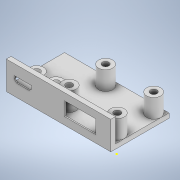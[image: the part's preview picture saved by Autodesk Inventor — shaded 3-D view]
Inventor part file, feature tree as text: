
AUTODESK INVENTOR PART (.ipt)
format: ipt  version: 2022 (Build 260153000, 153)  size: 289,280 bytes
history: native  units: mm
features: sketch x14, extrude x13
ambient origin geometry x8: Origin, YZ Plane, XZ Plane, XY Plane, X Axis, Y Axis, Z Axis, Center Point
bodies: Solid1 (feature_tree)
feature tree (27):
  extrude  "Extrusion1"  Depth=25.0mm
  extrude  "Extrusion2"  Depth=2.0mm
  extrude  "Extrusion3"  Depth=20.5mm
  extrude  "Extrusion4"  TaperAngle=0.0deg  [1 undecoded]
  extrude  "Extrusion5"  Depth=6.0mm
  extrude  "Extrusion6"  Depth=6.0mm
  extrude  "Extrusion7"  Depth=5.0mm
  extrude  "Extrusion8"  Depth=8.0mm TaperAngle=0.0deg
  extrude  "Extrusion9"  Depth=2.8mm
  extrude  "Extrusion10"  Depth=2.8mm
  extrude  "Extrusion11"  Depth=5.8mm
  extrude  "Extrusion12"  Depth=10.0mm TaperAngle=0.0deg
  extrude  "Extrusion13"  Depth=5.8mm
  sketch  "Sketch18"  dims[d36=1.0mm d37=8.3mm d38=10.0mm d39=0.0mm d40=100.0mm d41=0.0mm d42=16.0mm d43=1.3mm d44=1.5mm d45=1.5mm d46=0.0mm d49=18.0mm d50=2.0mm d51=0.0mm d52=2.0mm d53=0.0mm d54=14.0mm d55=10.0mm d56=10.0mm d57=8.3mm d58=6.0mm d59=6.0mm d60=2.85mm d61=1.9mm d62=0.0mm d63=3.0mm d64=3.0mm d65=4.0mm d66=0.0mm d68=7.4mm d69=2.3mm d70=2.65mm d71=1.4mm d75=1.0mm d76=1.0mm d77=135.0deg d78=4.0mm d79=0.0mm d80=1.6mm d81=8.0mm d82=1.0mm d83=1.0mm d84=1.0mm d85=1.5mm d86=0.0mm]
  sketch  "Sketch1"  dims[d0=30.0mm d1=25.0mm]
  sketch  "Sketch2"  dims[d2=2.0mm d3=0.0mm d4=15.5mm]
  sketch  "Sketch3"  dims[d5=15.5mm d6=20.5mm]
  sketch  "Sketch4"  dims[d7=20.5mm d8=0.0mm]
  sketch  "Sketch5"  dims[d9=0.0mm d10=6.0mm]
  sketch  "Sketch6"  dims[d11=6.0mm d12=6.0mm]
  sketch  "Sketch7"  dims[d13=6.0mm d14=5.0mm]
  sketch  "Sketch12"  dims[d15=3.5mm d16=8.0mm d17=0.0mm]
  sketch  "Sketch13"  dims[d18=2.8mm d19=2.8mm]
  sketch  "Sketch14"  dims[d20=2.8mm d21=2.8mm]
  sketch  "Sketch15"  dims[d22=4.0mm d23=0.0mm d28=5.8mm]
  sketch  "Sketch16"  dims[d29=2.0mm d30=10.0mm d31=0.0mm]
  sketch  "Sketch17"  dims[d32=13.4mm d33=5.8mm]
note: 1 required parameter value undecoded (feature->parameter linkage not recoverable at this tier; creation-order binding heuristic only, values carry confidence <= 0.55)
